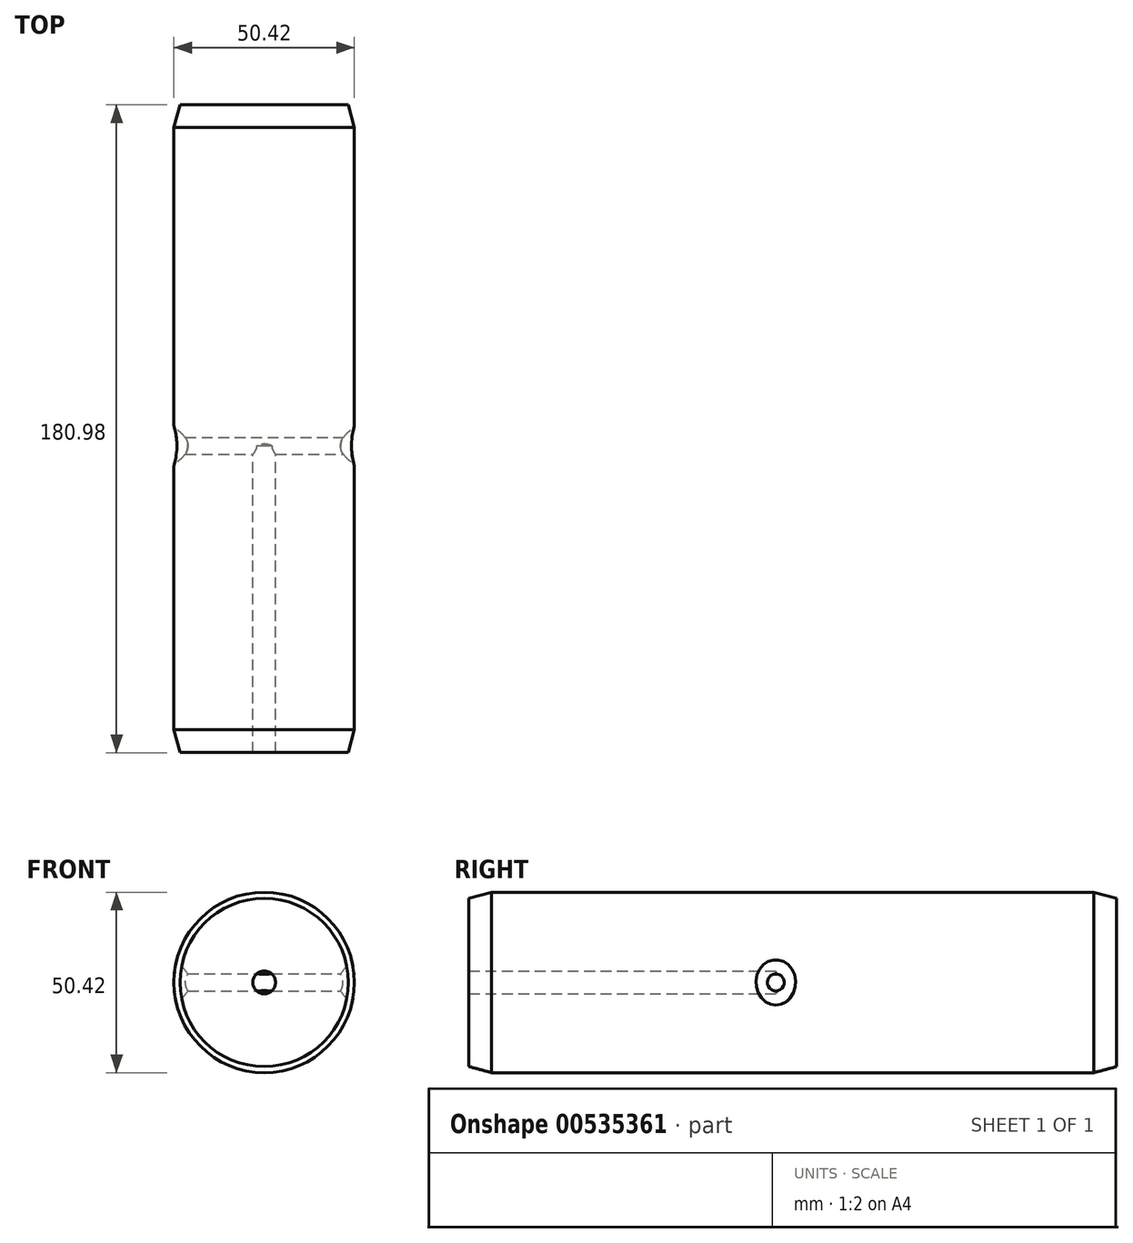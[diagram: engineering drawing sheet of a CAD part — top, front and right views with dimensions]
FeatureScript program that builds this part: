
annotation { "Feature Type Name" : "Feature", "Feature Type Description" : "" }
export const myFeature = defineFeature(function(context is Context, id is Id, definition is map)
    precondition{}
    {
        {
            var Q0;
            Q0=qCreatedBy(makeId("Front.planeOp"),FACE);
            var sketch = newSketch(context, id + "F0", { "sketchPlane" : qUnion([Q0])});
            skCircle(sketch, "E0", {"center": v(0, 0) * mm, "radius": 25.2 * mm});
            skSolve(sketch);
        }
        {
            var Q0;
            Q0=qSketchRegion(id+"F0",true);
            extrude(context, id + "F1", {"entities" : qUnion([Q0]), "depth" : 180.97 * mm, "offsetDistance" : 25.4 * mm});
        }
        {
            var Q0;
            Q0=makeQuery(id+"F1.opExtrude","CAP_EDGE",EDGE,{"disambiguationData":[OSD([sQuery(id+"F0.wireOp",EDGE,"E0")])],"isStart":false});
            var Q1;
            Q1=makeQuery(id+"F1.opExtrude","CAP_EDGE",EDGE,{"disambiguationData":[OSD([sQuery(id+"F0.wireOp",EDGE,"E0")])],"isStart":true});
            chamfer(context, id + "F2", {"entities" : qUnion([Q0, Q1]), "chamferType" : ChamferType.OFFSET_ANGLE, "width" : 6.35 * mm, "oppositeDirection" : true, "angle" : 15 * degree, "tangentPropagation" : true});
        }
        {
            var Q0;
            Q0=makeQuery(id+"F1.opExtrude","CAP_FACE",FACE,{"disambiguationData":[OSD([sQuery(id+"F0.wireOp",EDGE,"E0")])],"isStart":false});
            var sketch = newSketch(context, id + "F3", { "sketchPlane" : qUnion([Q0])});
            skPoint(sketch, "E1", {"position": v(0, 0) * mm});
            skSolve(sketch);
        }
        {
            var Q0;
            Q0=sQuery(id+"F3.wireOp",VERTEX,"E1");
            var Q1;
            Q1=makeQuery(id+"F1.opExtrude","SWEPT_BODY",BODY,{"disambiguationData":[OSD([sQuery(id+"F0.wireOp",EDGE,"E0")])]});
            hole(context, id + "F4", {"style" : HoleStyle.SIMPLE, "endStyle" : HoleEndStyle.BLIND, "holeDiameter" : 6.35 * mm, "holeDepth" : 85.72 * mm, "isTappedThrough" : true, "tappedDepth" : 12.7 * mm, "tapClearance" : 3, "startFromSketch" : true, "locations" : qUnion([Q0]), "scope" : qUnion([Q1])});
        }
        {
            var Q0;
            Q0=qCreatedBy(makeId("Right.planeOp"),FACE);
            var sketch = newSketch(context, id + "F5", { "sketchPlane" : qUnion([Q0])});
            skCircle(sketch, "E2", {"center": v(-95.25, 0) * mm, "radius": 2.37 * mm});
            skSolve(sketch);
        }
        {
            var Q0;
            Q0 = qSketchRegion(id + "F5", true);
            extrude(context, id + "F6", {"entities" : qUnion([Q0]), "operationType" : NewBodyOperationType.REMOVE, "endBound" : BoundingType.THROUGH_ALL, "oppositeDirection" : true, "depth" : 25.4 * mm, "offsetDistance" : 25.4 * mm, "hasSecondDirection" : true, "secondDirectionBound" : BoundingType.THROUGH_ALL, "secondDirectionOppositeDirection" : false, "secondDirectionDepth" : 25.4 * mm});
        }
        {
            var Q0;
            Q0=makeQuery(id+"F6.boolean.opBoolean","INTERSECT",EDGE,{"disambiguationData":[OD(1.0)],"derivedFrom":[makeQuery(id+"F1.opExtrude","SWEPT_FACE",FACE,{"disambiguationData":[OSD([sQuery(id+"F0.wireOp",EDGE,"E0")])]}),makeQuery(id+"F6.opExtrude","SWEPT_FACE",FACE,{"disambiguationData":[OSD([sQuery(id+"F5.wireOp",EDGE,"E2")])]})]});
            var Q1;
            Q1=makeQuery(id+"F6.boolean.opBoolean","INTERSECT",EDGE,{"disambiguationData":[OD(0.0)],"derivedFrom":[makeQuery(id+"F1.opExtrude","SWEPT_FACE",FACE,{"disambiguationData":[OSD([sQuery(id+"F0.wireOp",EDGE,"E0")])]}),makeQuery(id+"F6.opExtrude","SWEPT_FACE",FACE,{"disambiguationData":[OSD([sQuery(id+"F5.wireOp",EDGE,"E2")])]})]});
            chamfer(context, id + "F7", {"entities" : qUnion([Q0, Q1]), "width" : 3.17 * mm, "tangentPropagation" : true});
        }
    });
